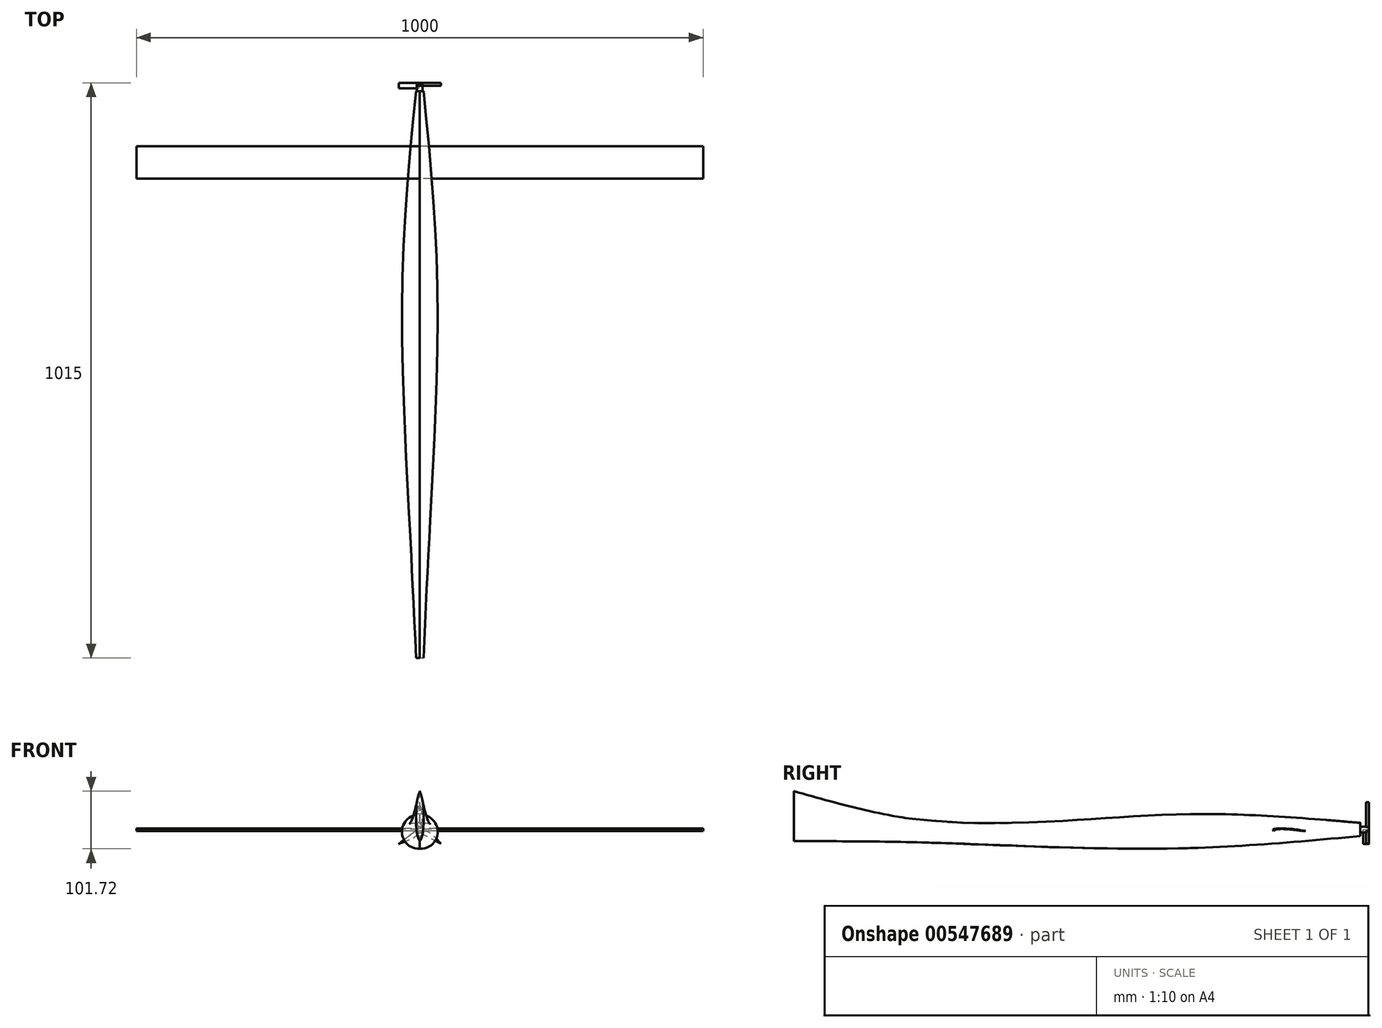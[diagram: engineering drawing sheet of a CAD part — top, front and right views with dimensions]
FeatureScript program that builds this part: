
annotation { "Feature Type Name" : "Feature", "Feature Type Description" : "" }
export const myFeature = defineFeature(function(context is Context, id is Id, definition is map)
    precondition{}
    {
        {
            var Q0;
            Q0=qCreatedBy(makeId("Front.planeOp"),FACE);
            var sketch = newSketch(context, id + "F0", { "sketchPlane" : qUnion([Q0])});
            skFitSpline(sketch, "E0", {"points": [v(0, 14.51) * mm, v(-5.67, 12.8) * mm, v(-4.35, -5.68) * mm, v(0, -8.71) * mm], "startDerivative": vector(-24.92, 1.93) * mm, "endDerivative": vector(18.37, -4.67) * mm});
            skLineSegment(sketch, "E1", {"start": v(0, -8.71) * mm, "end": v(0, 14.51) * mm});
            skSolve(sketch);
        }
        {
            var Q0;
            Q0=qCreatedBy(makeId("Front.planeOp"),FACE);
            cPlane(context, id + "F1", {"entities" : qUnion([Q0]), "cplaneType" : CPlaneType.OFFSET, "offset" : 300 * mm, "width" : 150 * mm, "height" : 150 * mm});
        }
        {
            var Q0;
            Q0=qCreatedBy(id+"F1.planeOp",FACE);
            var sketch = newSketch(context, id + "F2", { "sketchPlane" : qUnion([Q0])});
            skCircle(sketch, "E2", {"center": v(0, 0) * mm, "radius": 30 * mm});
            skLineSegment(sketch, "E3", {"start": v(0, -30) * mm, "end": v(0, 30) * mm});
            skSolve(sketch);
        }
        {
            var Q0;
            Q0=qCreatedBy(makeId("Front.planeOp"),FACE);
            cPlane(context, id + "F3", {"entities" : qUnion([Q0]), "cplaneType" : CPlaneType.OFFSET, "offset" : 800 * mm, "width" : 150 * mm, "height" : 150 * mm});
        }
        {
            var Q0;
            Q0=qCreatedBy(id+"F3.planeOp",FACE);
            var sketch = newSketch(context, id + "F4", { "sketchPlane" : qUnion([Q0])});
            skFitSpline(sketch, "E4", {"points": [v(0, 22.69) * mm, v(-14.56, 18.54) * mm, v(-9.22, -15.23) * mm, v(0, -19.38) * mm], "startDerivative": vector(-59.8, 3.83) * mm, "endDerivative": vector(38.96, -2.01) * mm});
            skLineSegment(sketch, "E5", {"start": v(0, -19.38) * mm, "end": v(0, 22.69) * mm});
            skSolve(sketch);
        }
        {
            var Q0;
            Q0=qCreatedBy(makeId("Front.planeOp"),FACE);
            cPlane(context, id + "F5", {"entities" : qUnion([Q0]), "cplaneType" : CPlaneType.OFFSET, "offset" : 1000 * mm, "width" : 150 * mm, "height" : 150 * mm});
        }
        {
            var Q0;
            Q0=qCreatedBy(id+"F5.planeOp",FACE);
            var sketch = newSketch(context, id + "F6", { "sketchPlane" : qUnion([Q0])});
            skFitSpline(sketch, "E6", {"points": [v(0, -17.78) * mm, v(-4.65, -6.18) * mm, v(-5.42, 48.81) * mm, v(0, 70.5) * mm], "startDerivative": vector(-22.95, 37.34) * mm, "endDerivative": vector(20.84, 57.52) * mm});
            skLineSegment(sketch, "E7", {"start": v(0, -17.78) * mm, "end": v(0, 70.5) * mm});
            skSolve(sketch);
        }
        {
            var Q0;
            Q0=makeQuery(id+"F0.imprint","IMPRINT",FACE,{"disambiguationData":[TD([[makeQuery(id+"F0.imprint","IMPRINT",EDGE,{"derivedFrom":sQuery(id+"F0.wireOp",EDGE,"E0")}),1.0]])]});
            var Q1;
            {var subQ0=sQuery(id+"F2.wireOp",EDGE,"E3");Q1=makeQuery(id+"F2.imprint","IMPRINT",FACE,{"disambiguationData":[TD([[makeQuery(id+"F2.imprint","IMPRINT",EDGE,{"derivedFrom":subQ0}),1.0]])]});}
            var Q2;
            Q2=makeQuery(id+"F4.imprint","IMPRINT",FACE,{"disambiguationData":[TD([[makeQuery(id+"F4.imprint","IMPRINT",EDGE,{"derivedFrom":sQuery(id+"F4.wireOp",EDGE,"E4")}),1.0]])]});
            var Q3;
            Q3=makeQuery(id+"F6.imprint","IMPRINT",FACE,{"disambiguationData":[TD([[makeQuery(id+"F6.imprint","IMPRINT",EDGE,{"derivedFrom":sQuery(id+"F6.wireOp",EDGE,"E6")}),-1.0]])]});
            loft(context, id + "F7", {"sheetProfilesArray" : [{ "sheetProfileEntities" : qUnion([Q0]) }, { "sheetProfileEntities" : qUnion([Q1]) }, { "sheetProfileEntities" : qUnion([Q2]) }, { "sheetProfileEntities" : qUnion([Q3]) }]});
        }
        {
            var Q0;
            Q0=makeQuery(id+"F7.opLoft","SWEPT_BODY",BODY,{"disambiguationData":[OSD([makeQuery(id+"F0.imprint","IMPRINT",FACE,{"disambiguationData":[TD([[makeQuery(id+"F0.imprint","IMPRINT",EDGE,{"derivedFrom":sQuery(id+"F0.wireOp",EDGE,"E0")}),1.0]])]}),sQuery(id+"F2.wireOp",EDGE,"E3"),sQuery(id+"F4.wireOp",EDGE,"E4"),makeQuery(id+"F6.imprint","IMPRINT",FACE,{"disambiguationData":[TD([[makeQuery(id+"F6.imprint","IMPRINT",EDGE,{"derivedFrom":sQuery(id+"F6.wireOp",EDGE,"E6")}),-1.0]])]})])]});
            var Q1;
            {var subQ0=sQuery(id+"F2.wireOp",EDGE,"E3");var subQ1=sQuery(id+"F2.wireOp",EDGE,"E2");var subQ2=sQuery(id+"F0.wireOp",EDGE,"E1");var subQ3=sQuery(id+"F0.wireOp",EDGE,"E0");Q1=makeQuery(id+"F7.opLoft","SWEPT_FACE",FACE,{"disambiguationData":[OSD([subQ3,subQ2,subQ1,subQ0]),TDD([makeQuery(id+"F0.imprint","INTERSECT",VERTEX,{"disambiguationData":[OD(0.0)],"derivedFrom":[subQ3,subQ2]}),makeQuery(id+"F0.imprint","INTERSECT",VERTEX,{"disambiguationData":[OD(1.0)],"derivedFrom":[subQ3,subQ2]}),makeQuery(id+"F0.imprint","IMPRINT",EDGE,{"derivedFrom":subQ2}),makeQuery(id+"F2.imprint","INTERSECT",VERTEX,{"disambiguationData":[OD(0.0)],"derivedFrom":[subQ1,subQ0]}),makeQuery(id+"F2.imprint","INTERSECT",VERTEX,{"disambiguationData":[OD(1.0)],"derivedFrom":[subQ1,subQ0]}),makeQuery(id+"F2.imprint","IMPRINT",EDGE,{"derivedFrom":subQ0})])]});}
            mirror(context, id + "F8", {"operationType" : NewBodyOperationType.ADD, "entities" : qUnion([Q0]), "mirrorPlane" : qUnion([Q1])});
        }
        {
            var Q0;
            Q0=qCreatedBy(makeId("Right.planeOp"),FACE);
            var sketch = newSketch(context, id + "F9", { "sketchPlane" : qUnion([Q0])});
            skFitSpline(sketch, "E8", {"points": [v(-96.92, 0) * mm, v(-118.74, 3.52) * mm, v(-147.6, 4.3) * mm, v(-154.36, 2.58) * mm, v(-153.42, 0) * mm], "startDerivative": vector(-61.56, 12.33) * mm, "endDerivative": vector(15.74, -24.7) * mm});
            skFitSpline(sketch, "E9", {"points": [v(-96.92, 0) * mm, v(-103.76, 0.5) * mm, v(-118.8, 2.35) * mm, v(-147.84, 3) * mm, v(-153.42, 0) * mm], "startDerivative": vector(-35.64, 1.94) * mm, "endDerivative": vector(-22.91, -20.2) * mm});
            skSolve(sketch);
        }
        {
            var Q0;
            Q0=makeQuery(id+"F9.imprint","IMPRINT",FACE,{"disambiguationData":[TD([[makeQuery(id+"F9.imprint","IMPRINT",EDGE,{"derivedFrom":sQuery(id+"F9.wireOp",EDGE,"E8")}),1.0]])]});
            extrude(context, id + "F10", {"entities" : qUnion([Q0]), "endBound" : BoundingType.SYMMETRIC, "depth" : 1000 * mm, "offsetDistance" : 25 * mm});
        }
        {
            var Q0;
            {var subQ0=makeQuery(id+"F7.opLoft","CAP_FACE",FACE,{"disambiguationData":[OSD([makeQuery(id+"F0.imprint","IMPRINT",FACE,{"disambiguationData":[TD([[makeQuery(id+"F0.imprint","IMPRINT",EDGE,{"derivedFrom":sQuery(id+"F0.wireOp",EDGE,"E0")}),1.0]])]})])],"isStart":true});Q0=makeQuery(id+"F8.boolean.opBoolean","MERGE",FACE,{"derivedFrom":[subQ0,makeQuery(id+"F8.opPattern","COPY",FACE,{"derivedFrom":subQ0,"instanceName":"1"})]});}
            var sketch = newSketch(context, id + "F11", { "sketchPlane" : qUnion([Q0])});
            skCircle(sketch, "E10", {"center": v(0, 2.78) * mm, "radius": 5 * mm});
            skFitSpline(sketch, "E11", {"points": [v(1.63, 7.5) * mm, v(4.6, 17.9) * mm, v(0, 28.76) * mm], "startDerivative": vector(9.76, 21.26) * mm, "endDerivative": vector(-12.87, 21.24) * mm});
            skLineSegment(sketch, "E12", {"start": v(0, 28.76) * mm, "end": v(0, 7.78) * mm});
            skSolve(sketch);
        }
        {
            var Q0;
            Q0=makeQuery(id+"F11.imprint","IMPRINT",FACE,{"disambiguationData":[TD([[makeQuery(id+"F11.imprint","IMPRINT",EDGE,{"derivedFrom":sQuery(id+"F11.wireOp",EDGE,"E10")}),1.0]])]});
            extrude(context, id + "F12", {"entities" : qUnion([Q0]), "operationType" : NewBodyOperationType.ADD, "depth" : 15 * mm, "offsetDistance" : 25 * mm});
        }
        {
            var Q0;
            {var subQ0=sQuery(id+"F11.wireOp",EDGE,"E11");var subQ1=sQuery(id+"F11.wireOp",EDGE,"E10");var subQ2=makeQuery(id+"F11.imprint","INTERSECT",VERTEX,{"derivedFrom":[subQ1,subQ0]});Q0=makeQuery(id+"F11.imprint","IMPRINT",FACE,{"disambiguationData":[TD([[makeQuery(id+"F11.imprint","IMPRINT",EDGE,{"disambiguationData":[TD([[subQ2,-1.0]])],"derivedFrom":subQ1}),-1.0]])]});}
            extrude(context, id + "F13", {"entities" : qUnion([Q0]), "depth" : 10 * mm, "offsetDistance" : 25 * mm});
        }
        {
            var Q0;
            Q0=makeQuery(id+"F13.opExtrude","SWEPT_BODY",BODY,{"disambiguationData":[OSD([sQuery(id+"F0.wireOp",EDGE,"E0"),sQuery(id+"F0.wireOp",EDGE,"E1"),sQuery(id+"F11.wireOp",EDGE,"E10"),sQuery(id+"F11.wireOp",EDGE,"E11"),sQuery(id+"F11.wireOp",EDGE,"E12")])]});
            deleteBodies(context, id + "F14", {"entities" : qUnion([Q0])});
        }
        {
            var Q0;
            Q0=makeQuery(id+"F12.opExtrude","CAP_FACE",FACE,{"disambiguationData":[OSD([sQuery(id+"F11.wireOp",EDGE,"E10")])],"isStart":false});
            var sketch = newSketch(context, id + "F15", { "sketchPlane" : qUnion([Q0])});
            skFitSpline(sketch, "E13", {"points": [v(2.09, 7.33) * mm, v(4.38, 18) * mm, v(0, 50.78) * mm], "startDerivative": vector(7.9, 21.78) * mm, "endDerivative": vector(-12.02, 20.59) * mm});
            skLineSegment(sketch, "E14", {"start": v(0, 50.78) * mm, "end": v(0, 7.78) * mm});
            skLineSegment(sketch, "E15", {"start": v(0, 7.78) * mm, "end": v(2.09, 7.33) * mm});
            skFitSpline(sketch, "E16", {"points": [v(4.15, 0) * mm, v(7.73, -9.82) * mm, v(37.13, -22.64) * mm], "startDerivative": vector(-34.29, -18.3) * mm, "endDerivative": vector(54.37, -21.29) * mm});
            skFitSpline(sketch, "E17", {"points": [v(-4.15, 0) * mm, v(-14.8, -1.16) * mm, v(-37.37, -22.29) * mm], "startDerivative": vector(-37.55, 0) * mm, "endDerivative": vector(-38.08, -43.14) * mm});
            skLineSegment(sketch, "E18", {"start": v(0, -2.22) * mm, "end": v(-37.37, -22.29) * mm});
            skLineSegment(sketch, "E19", {"start": v(37.13, -22.64) * mm, "end": v(5, 2.89) * mm});
            skSolve(sketch);
        }
        {
            var Q0;
            Q0 = qSketchRegion(id + "F15", true);
            extrude(context, id + "F16", {"entities" : qUnion([Q0]), "oppositeDirection" : true, "depth" : 5 * mm, "offsetDistance" : 25 * mm});
        }
        {
            var Q0;
            Q0=makeQuery(id+"F16.opExtrude","SWEPT_BODY",BODY,{"disambiguationData":[OSD([sQuery(id+"F15.wireOp",EDGE,"E13"),sQuery(id+"F15.wireOp",EDGE,"E14"),sQuery(id+"F15.wireOp",EDGE,"E15")])]});
            var Q1;
            Q1=makeQuery(id+"F16.opExtrude","SWEPT_FACE",FACE,{"disambiguationData":[OSD([sQuery(id+"F15.wireOp",EDGE,"E14")])]});
            mirror(context, id + "F17", {"entities" : qUnion([Q0]), "mirrorPlane" : qUnion([Q1])});
        }
        {
            var Q0;
            {var subQ0=sQuery(id+"F15.wireOp",EDGE,"E17");Q0=makeQuery(id+"F15.imprint","IMPRINT",FACE,{"disambiguationData":[TD([[makeQuery(id+"F15.imprint","IMPRINT",EDGE,{"derivedFrom":subQ0}),1.0]])]});}
            extrude(context, id + "F18", {"entities" : qUnion([Q0]), "oppositeDirection" : true, "depth" : 5 * mm, "offsetDistance" : 25 * mm});
        }
        {
            var Q0;
            {var subQ0=sQuery(id+"F15.wireOp",EDGE,"E19");Q0=makeQuery(id+"F15.imprint","IMPRINT",FACE,{"disambiguationData":[TD([[makeQuery(id+"F15.imprint","IMPRINT",EDGE,{"derivedFrom":subQ0}),1.0]])]});}
            extrude(context, id + "F19", {"entities" : qUnion([Q0]), "oppositeDirection" : true, "depth" : 10 * mm, "offsetDistance" : 25 * mm});
        }
    });
